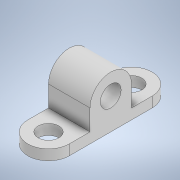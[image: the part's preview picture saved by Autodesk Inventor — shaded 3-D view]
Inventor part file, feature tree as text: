
AUTODESK INVENTOR PART (.ipt)
format: ipt  version: 2022 (Build 260153000, 153)  size: 133,632 bytes
history: native  units: mm
features: extrude x2, sketch x2, other x1
ambient origin geometry x8: Origin, YZ Plane, XZ Plane, XY Plane, X Axis, Y Axis, Z Axis, Center Point
bodies: Body1 (feature_tree)
feature tree (5):
  other  "Sólido1"
  extrude  "Extrusión1"  Depth=40.0mm
  extrude  "Extrusión2"  Depth=40.0mm
  sketch  "Boceto1"  dims[d0=40.0mm d1=40.0mm]
  sketch  "Boceto2"  dims[d3=20.0mm d4=40.0mm d6=20.0mm d7=40.0mm d8=10.0mm d9=0.0mm d11=40.0mm d12=20.0mm d13=40.0mm d14=0.0mm]
